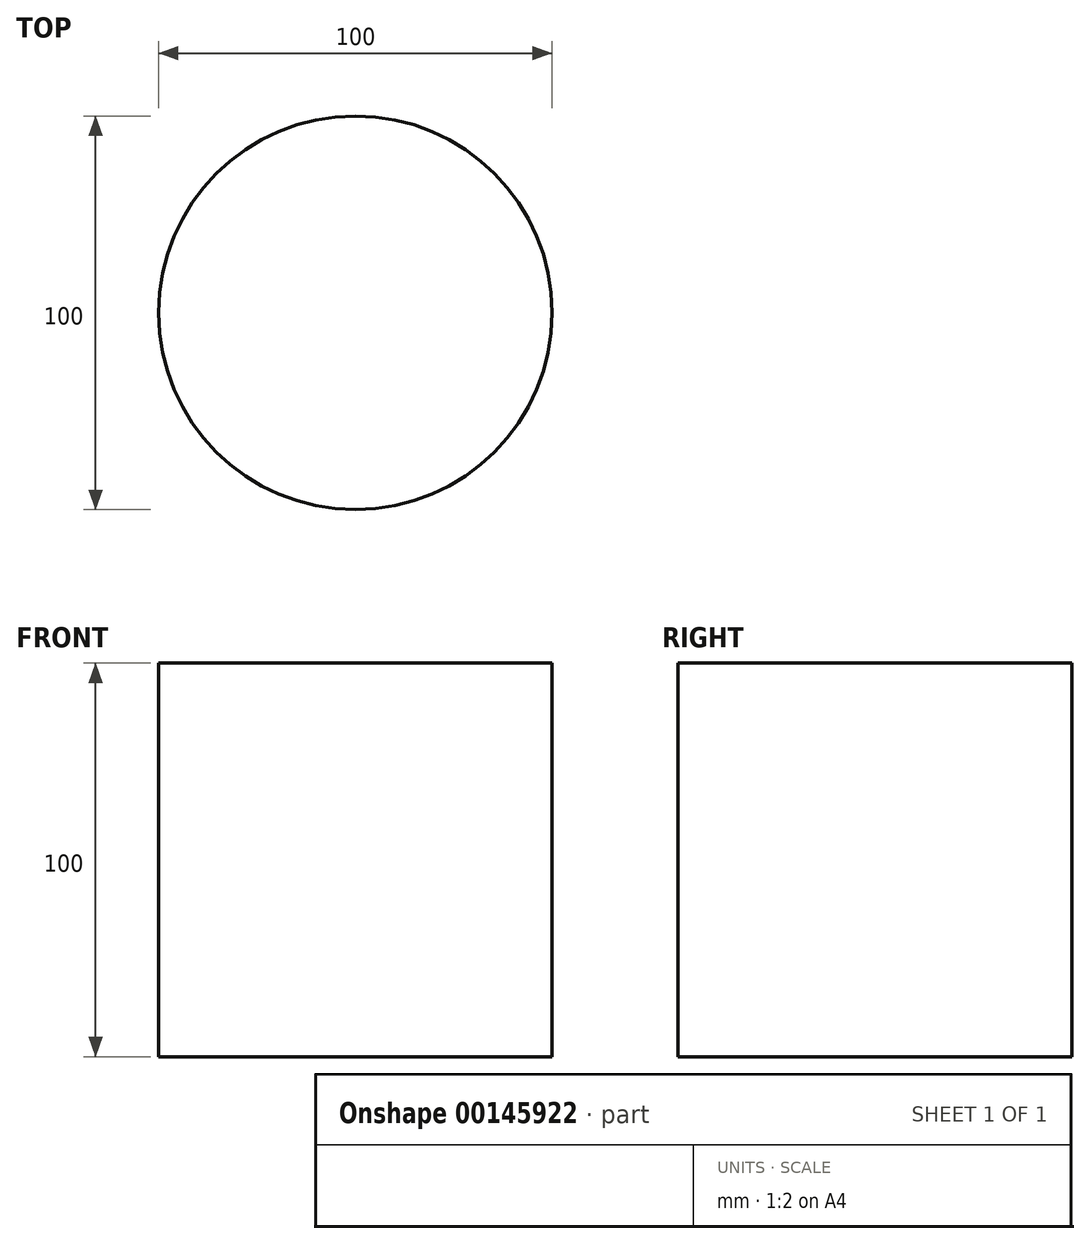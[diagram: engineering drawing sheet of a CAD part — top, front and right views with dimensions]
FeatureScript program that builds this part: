
annotation { "Feature Type Name" : "Feature", "Feature Type Description" : "" }
export const myFeature = defineFeature(function(context is Context, id is Id, definition is map)
    precondition{}
    {
        {
            var Q0;
            Q0=qCreatedBy(makeId("Top.planeOp"),FACE);
            var sketch = newSketch(context, id + "F0", { "sketchPlane" : qUnion([Q0])});
            skCircle(sketch, "E0", {"center": v(0, 0) * mm, "radius": 50 * mm});
            skSolve(sketch);
        }
        {
            var Q0;
            Q0 = qSketchRegion(id + "F0", true);
            extrude(context, id + "F1", {"entities" : qUnion([Q0]), "endBound" : BoundingType.SYMMETRIC, "depth" : 100 * mm});
        }
    });
